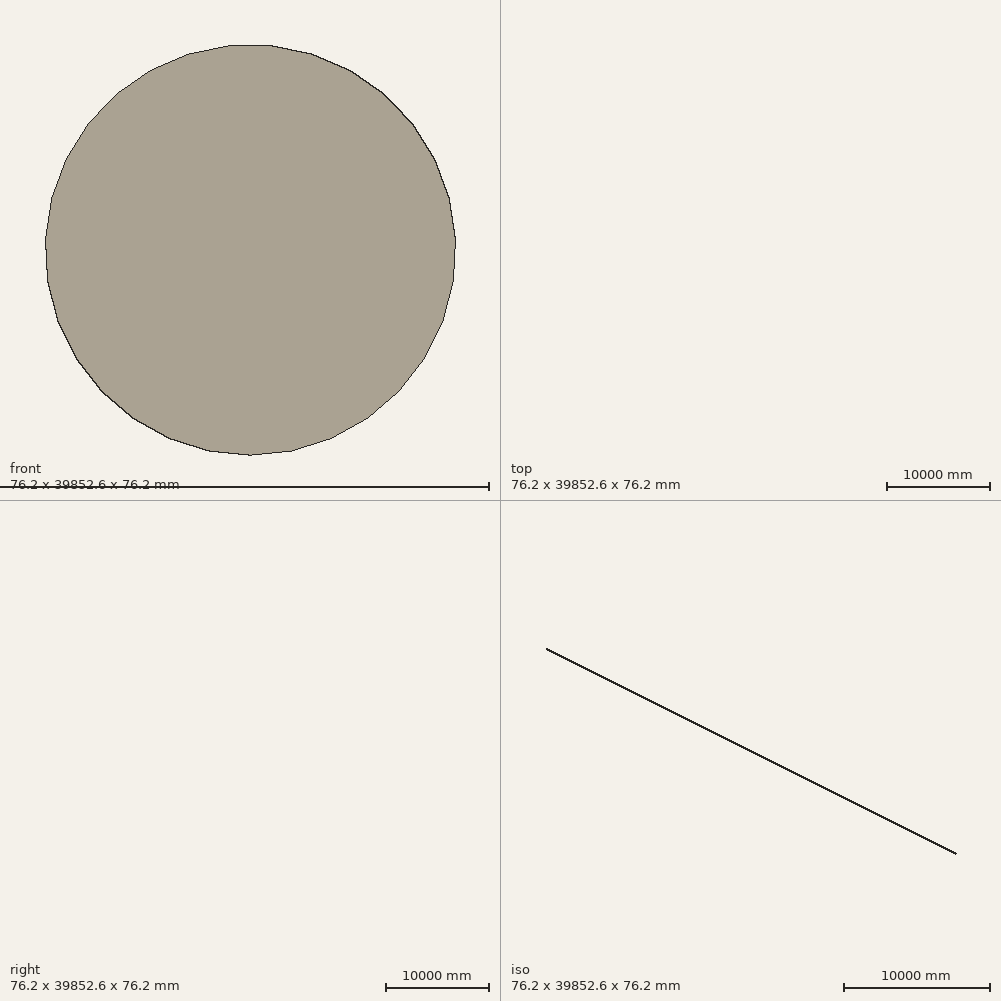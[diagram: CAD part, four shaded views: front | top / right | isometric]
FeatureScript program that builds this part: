
annotation { "Feature Type Name" : "Feature", "Feature Type Description" : "" }
export const myFeature = defineFeature(function(context is Context, id is Id, definition is map)
    precondition{}
    {
        {
            var Q0;
            Q0=qCreatedBy(makeId("Front.planeOp"),FACE);
            var sketch = newSketch(context, id + "F0", { "sketchPlane" : qUnion([Q0])});
            skCircle(sketch, "E0", {"center": v(0, 0) * mm, "radius": 38.1 * mm});
            skSolve(sketch);
        }
        {
            var Q0;
            Q0=makeQuery(id+"F0.imprint","IMPRINT",FACE,{"disambiguationData":[TD([[makeQuery(id+"F0.imprint","IMPRINT",EDGE,{"derivedFrom":sQuery(id+"F0.wireOp",EDGE,"E0")}),1.0]])]});
            extrude(context, id + "F1", {"entities" : qUnion([Q0]), "depth" : 39852.6 * mm});
        }
    });
